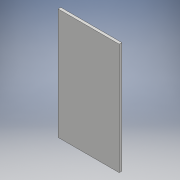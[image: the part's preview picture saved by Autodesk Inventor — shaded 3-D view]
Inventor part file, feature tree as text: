
AUTODESK INVENTOR PART (.ipt)
format: ipt  version: 2018 (Build 220112000, 112)  size: 90,624 bytes
history: native  units: mm
features: extrude x1, sketch x1
ambient origin geometry x8: Origin, YZ Plane, XZ Plane, XY Plane, X Axis, Y Axis, Z Axis, Center Point
bodies: Solid1 (feature_tree)
feature tree (2):
  extrude  "Extrusion1"  Depth=66.5mm
  sketch  "Sketch1"  dims[d0=36.5mm d1=66.5mm d2=1.6mm d3=0.0mm]
